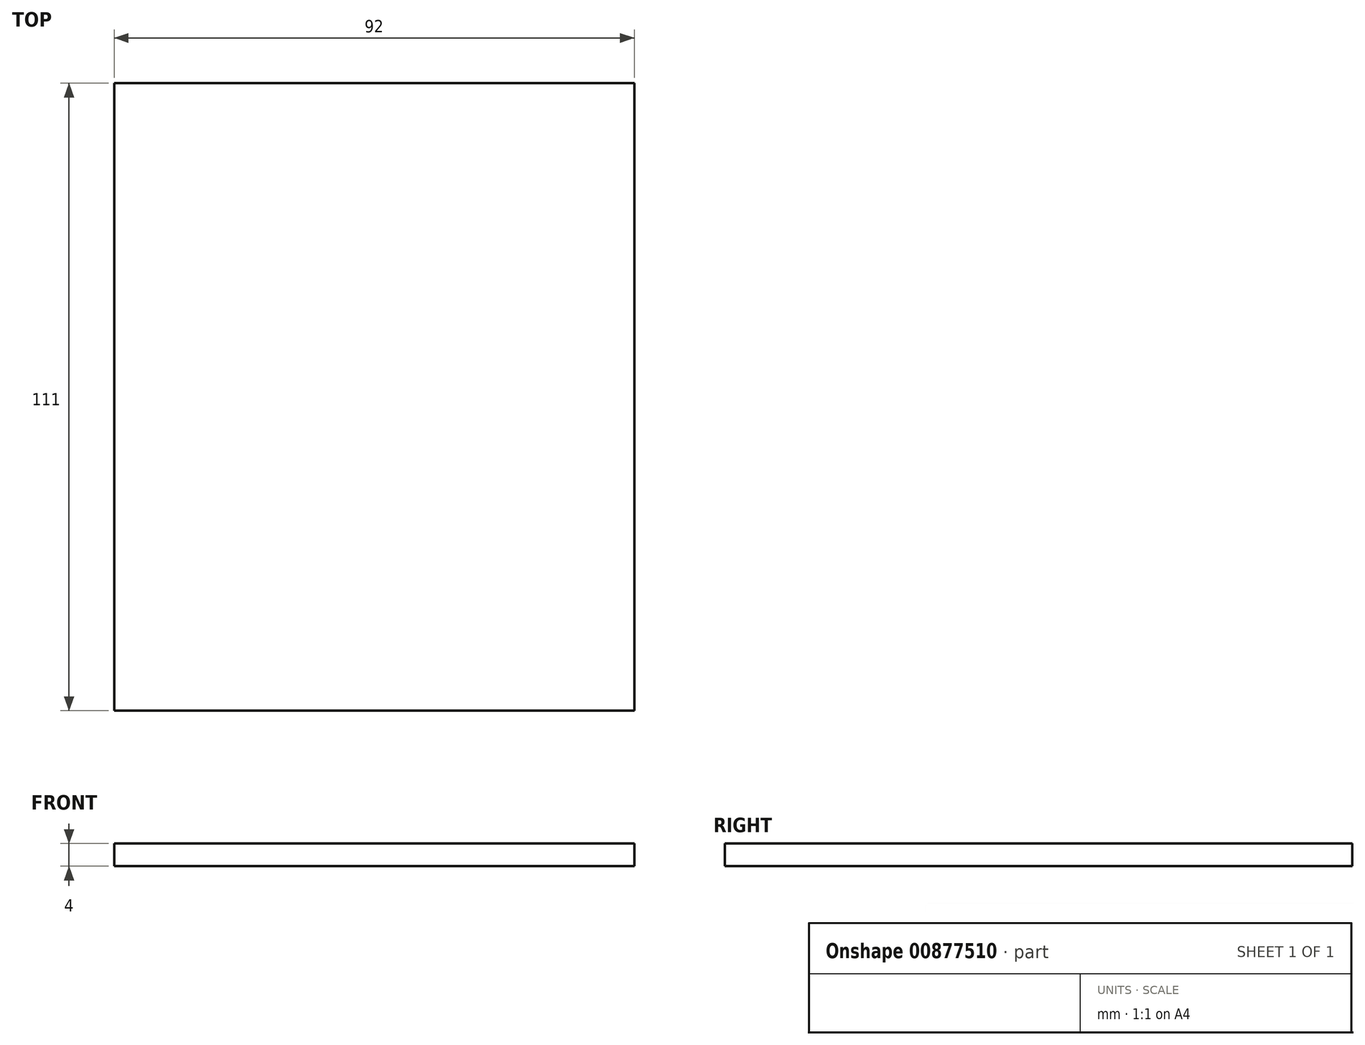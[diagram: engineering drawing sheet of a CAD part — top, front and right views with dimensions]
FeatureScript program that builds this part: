
annotation { "Feature Type Name" : "Feature", "Feature Type Description" : "" }
export const myFeature = defineFeature(function(context is Context, id is Id, definition is map)
    precondition{}
    {
        {
            var Q0;
            Q0=qCreatedBy(makeId("Top.planeOp"),FACE);
            var sketch = newSketch(context, id + "F0", { "sketchPlane" : qUnion([Q0])});
            skLineSegment(sketch, "E0.bottom", {"start": v(46, -55.5) * mm, "end": v(-46, -55.5) * mm});
            skLineSegment(sketch, "E0.top", {"start": v(46, 55.5) * mm, "end": v(-46, 55.5) * mm});
            skLineSegment(sketch, "E0.left", {"start": v(46, -55.5) * mm, "end": v(46, 55.5) * mm});
            skLineSegment(sketch, "E0.right", {"start": v(-46, -55.5) * mm, "end": v(-46, 55.5) * mm});
            skPoint(sketch, "E0.middle", {"position": v(0, 0) * mm});
            skSolve(sketch);
        }
        {
            var Q0;
            Q0=makeQuery(id+"F0.imprint","IMPRINT",FACE,{"disambiguationData":[TD([[makeQuery(id+"F0.imprint","IMPRINT",EDGE,{"derivedFrom":sQuery(id+"F0.wireOp",EDGE,"E0.bottom")}),-1.0]])]});
            extrude(context, id + "F1", {"entities" : qUnion([Q0]), "depth" : 4 * mm, "offsetDistance" : 25.4 * mm});
        }
    });
